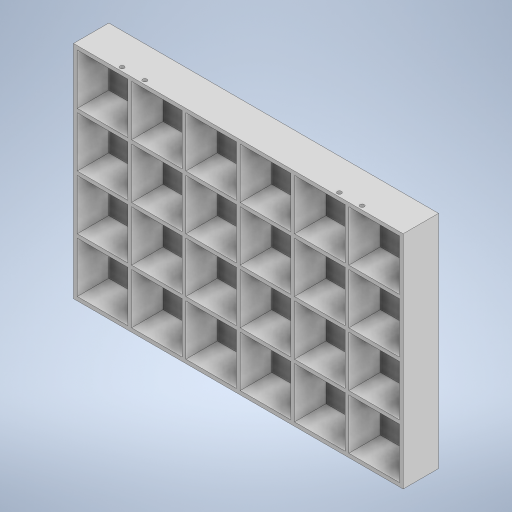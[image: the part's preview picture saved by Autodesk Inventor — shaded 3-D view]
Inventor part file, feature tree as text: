
AUTODESK INVENTOR PART (.ipt)
format: ipt  version: 2023.5 (Build 275446000, 446)  size: 425,472 bytes
history: native  units: in
note: dims shown in document units (in); Inventor stores cm internally (conversion verified against a paired STEP export)
features: extrude x3, sketch x3
ambient origin geometry x8: Origin, YZ Plane, XZ Plane, XY Plane, X Axis, Y Axis, Z Axis, Center Point
bodies: Solid1 (feature_tree)
feature tree (6):
  extrude  "Extrusion1"  Depth=6.8898in
  extrude  "Extrusion2"  TaperAngle=0.0deg  [1 undecoded]
  extrude  "Extrusion3"  Depth=0.1181in
  sketch  "Sketch1"  dims[d0=10.2756in d1=6.8898in]
  sketch  "Sketch2"  dims[d2=1.1024in d3=0.0in]
  sketch  "Sketch3"  dims[d4=1.5748in d5=0.1181in d6=0.1181in d7=1.5748in d8=2.3622in d10=1.6929in d11=1.5748in d13=1.6929in d16=0.9843in d17=0.0in d20=0.1181in d21=0.1299in d22=0.3543in d23=0.1299in d24=0.3543in d25=0.1299in d31=0.1299in d33=0.3937in d34=0.0in d35=0.7087in d36=1.3976in]
note: 1 required parameter value undecoded (feature->parameter linkage not recoverable at this tier; creation-order binding heuristic only, values carry confidence <= 0.55)
